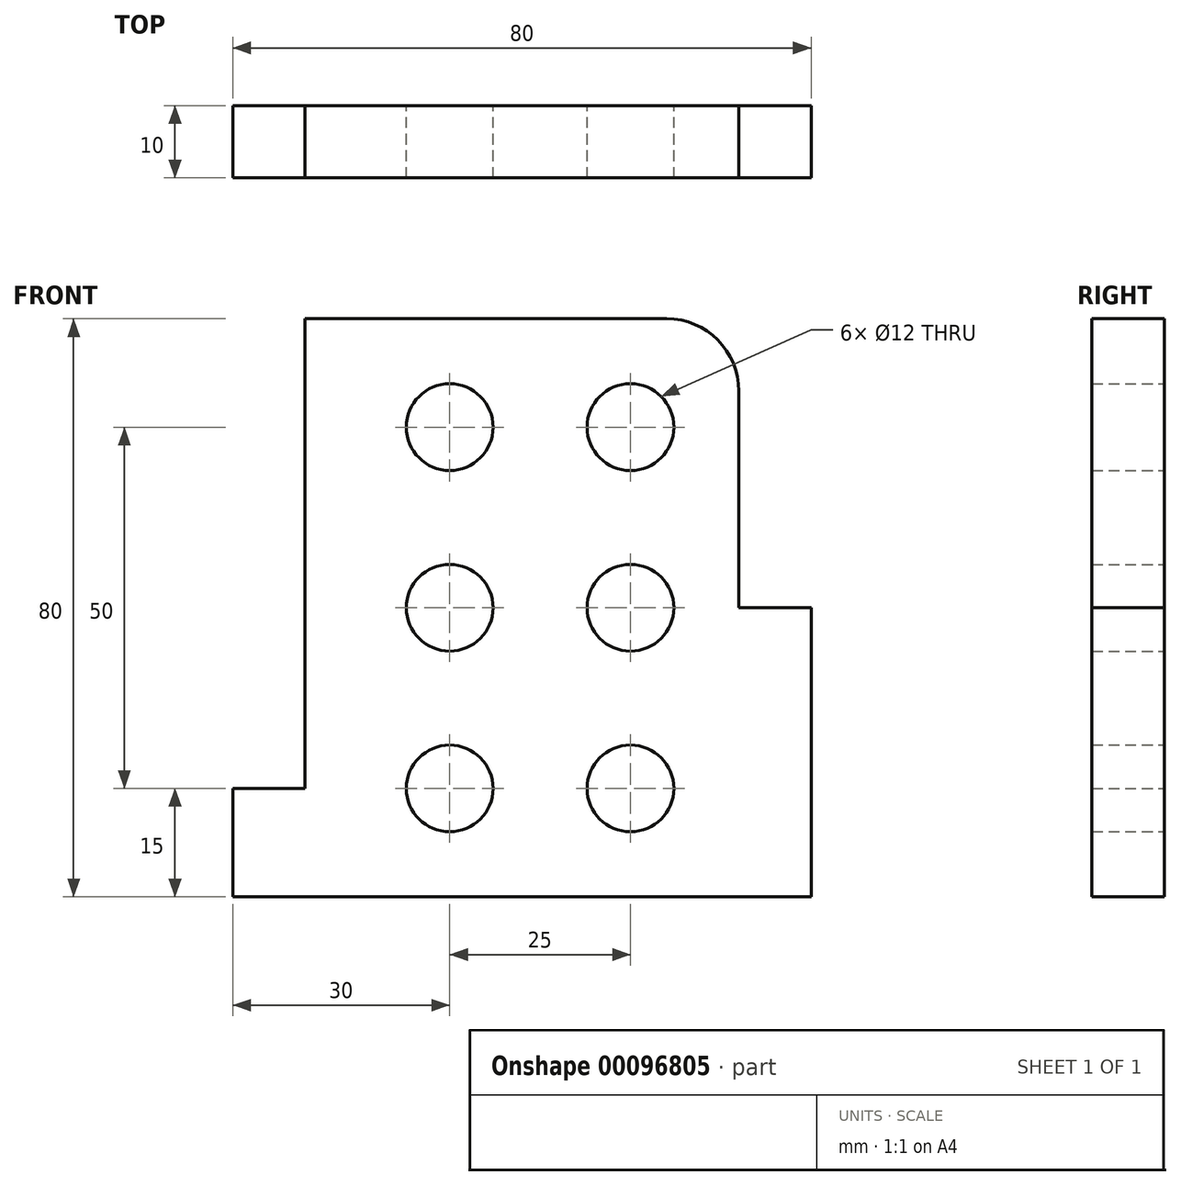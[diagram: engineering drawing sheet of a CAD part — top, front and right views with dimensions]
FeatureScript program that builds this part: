
annotation { "Feature Type Name" : "Feature", "Feature Type Description" : "" }
export const myFeature = defineFeature(function(context is Context, id is Id, definition is map)
    precondition{}
    {
        {
            var Q0;
            Q0=qCreatedBy(makeId("Front.planeOp"),FACE);
            var sketch = newSketch(context, id + "F0", { "sketchPlane" : qUnion([Q0])});
            skLineSegment(sketch, "E0", {"start": v(0, 0) * mm, "end": v(80, 0) * mm});
            skLineSegment(sketch, "E1", {"start": v(80, 0) * mm, "end": v(80, 40) * mm});
            skLineSegment(sketch, "E2", {"start": v(80, 40) * mm, "end": v(70, 40) * mm});
            skLineSegment(sketch, "E3", {"start": v(70, 40) * mm, "end": v(70, 70) * mm});
            skLineSegment(sketch, "E4", {"start": v(0, 0) * mm, "end": v(0, 15) * mm});
            skLineSegment(sketch, "E5", {"start": v(0, 15) * mm, "end": v(10, 15) * mm});
            skLineSegment(sketch, "E6", {"start": v(10, 15) * mm, "end": v(10, 80) * mm});
            skLineSegment(sketch, "E7", {"start": v(10, 80) * mm, "end": v(60, 80) * mm});
            skCircle(sketch, "E8", {"center": v(30, 15) * mm, "radius": 6 * mm});
            skCircle(sketch, "E9", {"center": v(30, 40) * mm, "radius": 6 * mm});
            skCircle(sketch, "E10", {"center": v(30, 65) * mm, "radius": 6 * mm});
            skCircle(sketch, "E11", {"center": v(55, 65) * mm, "radius": 6 * mm});
            skCircle(sketch, "E12", {"center": v(55, 40) * mm, "radius": 6 * mm});
            skCircle(sketch, "E13", {"center": v(55, 15) * mm, "radius": 6 * mm});
            skArc(sketch, "E14", {"start": v(60, 80) * mm, "mid": v(67.07, 77.07) * mm, "end": v(70, 70) * mm});
            skSolve(sketch);
        }
        {
            var Q0;
            Q0 = qSketchRegion(id + "F0", true);
            extrude(context, id + "F1", {"entities" : qUnion([Q0]), "depth" : 10 * mm});
        }
    });
